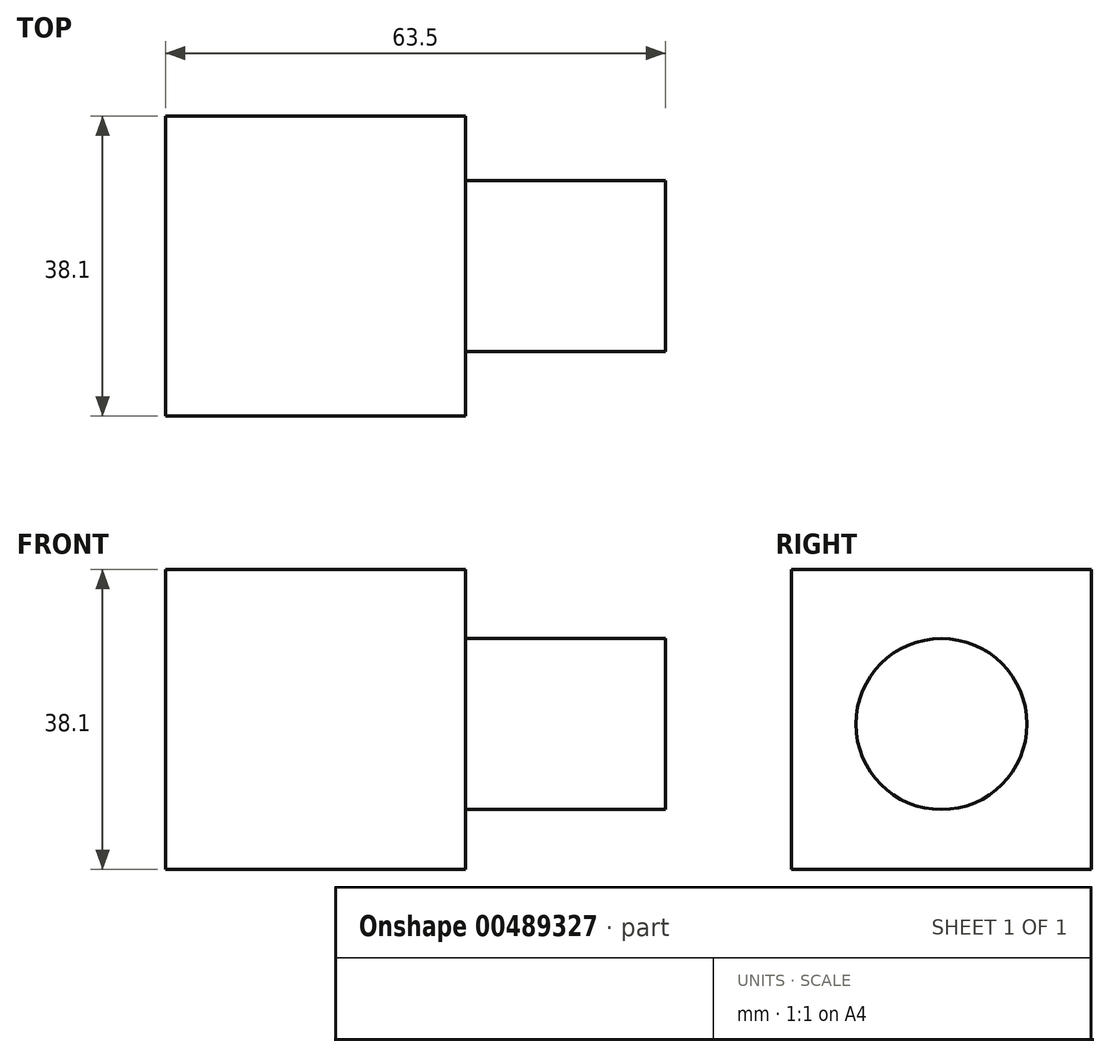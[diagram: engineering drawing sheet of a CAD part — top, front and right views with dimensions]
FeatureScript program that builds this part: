
annotation { "Feature Type Name" : "Feature", "Feature Type Description" : "" }
export const myFeature = defineFeature(function(context is Context, id is Id, definition is map)
    precondition{}
    {
        {
            var Q0;
            Q0=qCreatedBy(makeId("Front.planeOp"),FACE);
            var sketch = newSketch(context, id + "F0", { "sketchPlane" : qUnion([Q0])});
            skLineSegment(sketch, "E0.bottom", {"start": v(0, 0) * mm, "end": v(-38.1, 0) * mm});
            skLineSegment(sketch, "E0.top", {"start": v(0, 38.1) * mm, "end": v(-38.1, 38.1) * mm});
            skLineSegment(sketch, "E0.left", {"start": v(0, 0) * mm, "end": v(0, 38.1) * mm});
            skLineSegment(sketch, "E0.right", {"start": v(-38.1, 0) * mm, "end": v(-38.1, 38.1) * mm});
            skSolve(sketch);
        }
        {
            var Q0;
            Q0 = qSketchRegion(id + "F0", true);
            extrude(context, id + "F1", {"entities" : qUnion([Q0]), "endBound" : BoundingType.SYMMETRIC, "depth" : 38.1 * mm});
        }
        {
            var Q0;
            Q0=makeQuery(id+"F1.opExtrude","SWEPT_FACE",FACE,{"disambiguationData":[OSD([sQuery(id+"F0.wireOp",EDGE,"E0.left")])]});
            var sketch = newSketch(context, id + "F2", { "sketchPlane" : qUnion([Q0])});
            skCircle(sketch, "E1", {"center": v(0, 18.47) * mm, "radius": 10.86 * mm});
            skSolve(sketch);
        }
        {
            var Q0;
            Q0 = qSketchRegion(id + "F2", true);
            extrude(context, id + "F3", {"entities" : qUnion([Q0]), "operationType" : NewBodyOperationType.ADD, "depth" : 25.4 * mm});
        }
    });
